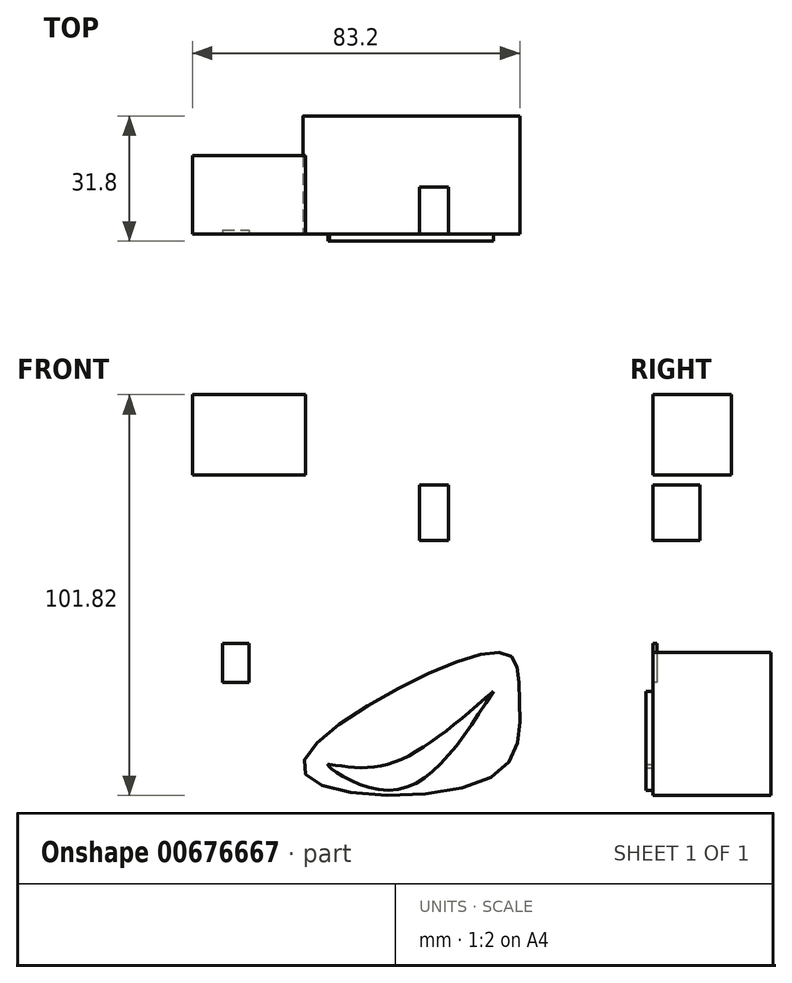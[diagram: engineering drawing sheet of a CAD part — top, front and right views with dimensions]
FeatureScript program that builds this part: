
annotation { "Feature Type Name" : "Feature", "Feature Type Description" : "" }
export const myFeature = defineFeature(function(context is Context, id is Id, definition is map)
    precondition{}
    {
        {
            var Q0;
            Q0=qCreatedBy(makeId("Front.planeOp"),FACE);
            var sketch = newSketch(context, id + "F0", { "sketchPlane" : qUnion([Q0])});
            skFitSpline(sketch, "E0", {"points": [v(0, -6.75) * mm, v(48.08, -6.93) * mm, v(54.26, 12.85) * mm, v(52.02, 23.45) * mm, v(24.46, 15.5) * mm, v(0, -6.75) * mm]});
            skSolve(sketch);
        }
        {
            var Q0;
            Q0 = qSketchRegion(id + "F0", true);
            extrude(context, id + "F1", {"entities" : qUnion([Q0]), "oppositeDirection" : true, "depth" : 30 * mm, "offsetDistance" : 25.4 * mm});
        }
        {
            var Q0;
            Q0=qCreatedBy(makeId("Front.planeOp"),FACE);
            var sketch = newSketch(context, id + "F2", { "sketchPlane" : qUnion([Q0])});
            skLineSegment(sketch, "E1.bottom", {"start": v(0, 69.27) * mm, "end": v(-28.73, 69.27) * mm});
            skLineSegment(sketch, "E1.top", {"start": v(0, 89.72) * mm, "end": v(-28.73, 89.72) * mm});
            skLineSegment(sketch, "E1.left", {"start": v(0, 69.27) * mm, "end": v(0, 89.72) * mm});
            skLineSegment(sketch, "E1.right", {"start": v(-28.73, 69.27) * mm, "end": v(-28.73, 89.72) * mm});
            skSolve(sketch);
        }
        {
            var Q0;
            Q0=makeQuery(id+"F2.imprint","IMPRINT",FACE,{"disambiguationData":[TD([[makeQuery(id+"F2.imprint","IMPRINT",EDGE,{"derivedFrom":sQuery(id+"F2.wireOp",EDGE,"E1.bottom")}),-1.0]])]});
            extrude(context, id + "F3", {"entities" : qUnion([Q0]), "oppositeDirection" : true, "depth" : 20 * mm, "offsetDistance" : 25 * mm});
        }
        {
            var Q0;
            Q0=qCreatedBy(makeId("Front.planeOp"),FACE);
            var sketch = newSketch(context, id + "F4", { "sketchPlane" : qUnion([Q0])});
            skLineSegment(sketch, "E2.bottom", {"start": v(28.96, 66.84) * mm, "end": v(36.27, 66.84) * mm});
            skLineSegment(sketch, "E2.top", {"start": v(28.96, 52.64) * mm, "end": v(36.27, 52.64) * mm});
            skLineSegment(sketch, "E2.left", {"start": v(28.96, 66.84) * mm, "end": v(28.96, 52.64) * mm});
            skLineSegment(sketch, "E2.right", {"start": v(36.27, 66.84) * mm, "end": v(36.27, 52.64) * mm});
            skSolve(sketch);
        }
        {
            var Q0;
            Q0 = qSketchRegion(id + "F4", true);
            extrude(context, id + "F5", {"entities" : qUnion([Q0]), "oppositeDirection" : true, "depth" : 12 * mm, "offsetDistance" : 25 * mm});
        }
        {
            var Q0;
            Q0=qCreatedBy(makeId("Front.planeOp"),FACE);
            var sketch = newSketch(context, id + "F6", { "sketchPlane" : qUnion([Q0])});
            skLineSegment(sketch, "E3.bottom", {"start": v(-21.09, 26.53) * mm, "end": v(-14.34, 26.53) * mm});
            skLineSegment(sketch, "E3.top", {"start": v(-21.09, 16.67) * mm, "end": v(-14.34, 16.67) * mm});
            skLineSegment(sketch, "E3.left", {"start": v(-21.09, 26.53) * mm, "end": v(-21.09, 16.67) * mm});
            skLineSegment(sketch, "E3.right", {"start": v(-14.34, 26.53) * mm, "end": v(-14.34, 16.67) * mm});
            skSolve(sketch);
        }
        {
            var Q0;
            Q0 = qSketchRegion(id + "F6", true);
            extrude(context, id + "F7", {"entities" : qUnion([Q0]), "oppositeDirection" : true, "depth" : 1 * mm, "offsetDistance" : 25 * mm});
        }
        {
            var Q0;
            Q0=qCreatedBy(makeId("Top.planeOp"),FACE);
            var sketch = newSketch(context, id + "F8", { "sketchPlane" : qUnion([Q0])});
            skFitSpline(sketch, "E4", {"points": [v(-77.38, -49.02) * mm, v(-66.82, -68.35) * mm, v(-32.77, -60.2) * mm, v(-65.3, -58.4) * mm, v(-78.6, -40.63) * mm, v(-77.38, -49.02) * mm]});
            skFitSpline(sketch, "E5", {"points": [v(-77.09, -50.05) * mm, v(-75.16, -60.09) * mm], "startDerivative": vector(1.94, -10.03) * mm, "endDerivative": vector(1.94, -10.03) * mm});
            skSolve(sketch);
        }
        {
            var Q0;
            Q0=sQuery(id+"F8.wireOp",EDGE,"E4");
            extrude(context, id + "F9", {"bodyType" : ToolBodyType.SURFACE, "surfaceEntities" : qUnion([Q0]), "depth" : 0.1 * mm, "offsetDistance" : 25 * mm});
        }
        {
            var Q0;
            Q0=makeQuery(id+"F1.opExtrude","CAP_FACE",FACE,{"disambiguationData":[OSD([sQuery(id+"F0.wireOp",EDGE,"E0")])],"isStart":true});
            var sketch = newSketch(context, id + "F10", { "sketchPlane" : qUnion([Q0])});
            skSolve(sketch);
        }
        {
            var Q0;
            Q0=makeQuery(id+"F10.imprint","IMPRINT",FACE,{"disambiguationData":[TD([[makeQuery(id+"F10.imprint","IMPRINT",EDGE,{"derivedFrom":makeQuery(id+"F1.opExtrude","CAP_EDGE",EDGE,{"disambiguationData":[OSD([sQuery(id+"F0.wireOp",EDGE,"E0")])],"isStart":true})}),1.0]])]});
            var sketch = newSketch(context, id + "F11", { "sketchPlane" : qUnion([Q0])});
            skFitSpline(sketch, "E6", {"points": [v(47.7, 14.37) * mm, v(21.27, -10.82) * mm, v(5.74, -4.37) * mm, v(6.05, -4.16) * mm], "startDerivative": vector(-42.56, -66.89) * mm, "endDerivative": vector(8.64, 1.98) * mm});
            skFitSpline(sketch, "E7", {"points": [v(47.7, 14.37) * mm, v(21.74, -3.95) * mm, v(6.05, -4.16) * mm], "startDerivative": vector(-46.02, -40.2) * mm, "endDerivative": vector(-36.74, 5.83) * mm});
            skSolve(sketch);
        }
        {
            var Q0;
            Q0=makeQuery(id+"F11.imprint","IMPRINT",FACE,{"disambiguationData":[TD([[makeQuery(id+"F11.imprint","IMPRINT",EDGE,{"derivedFrom":sQuery(id+"F11.wireOp",EDGE,"E6")}),-1.0]])]});
            extrude(context, id + "F12", {"entities" : qUnion([Q0]), "operationType" : NewBodyOperationType.ADD, "depth" : 1.8 * mm, "offsetDistance" : 25 * mm});
        }
    });
